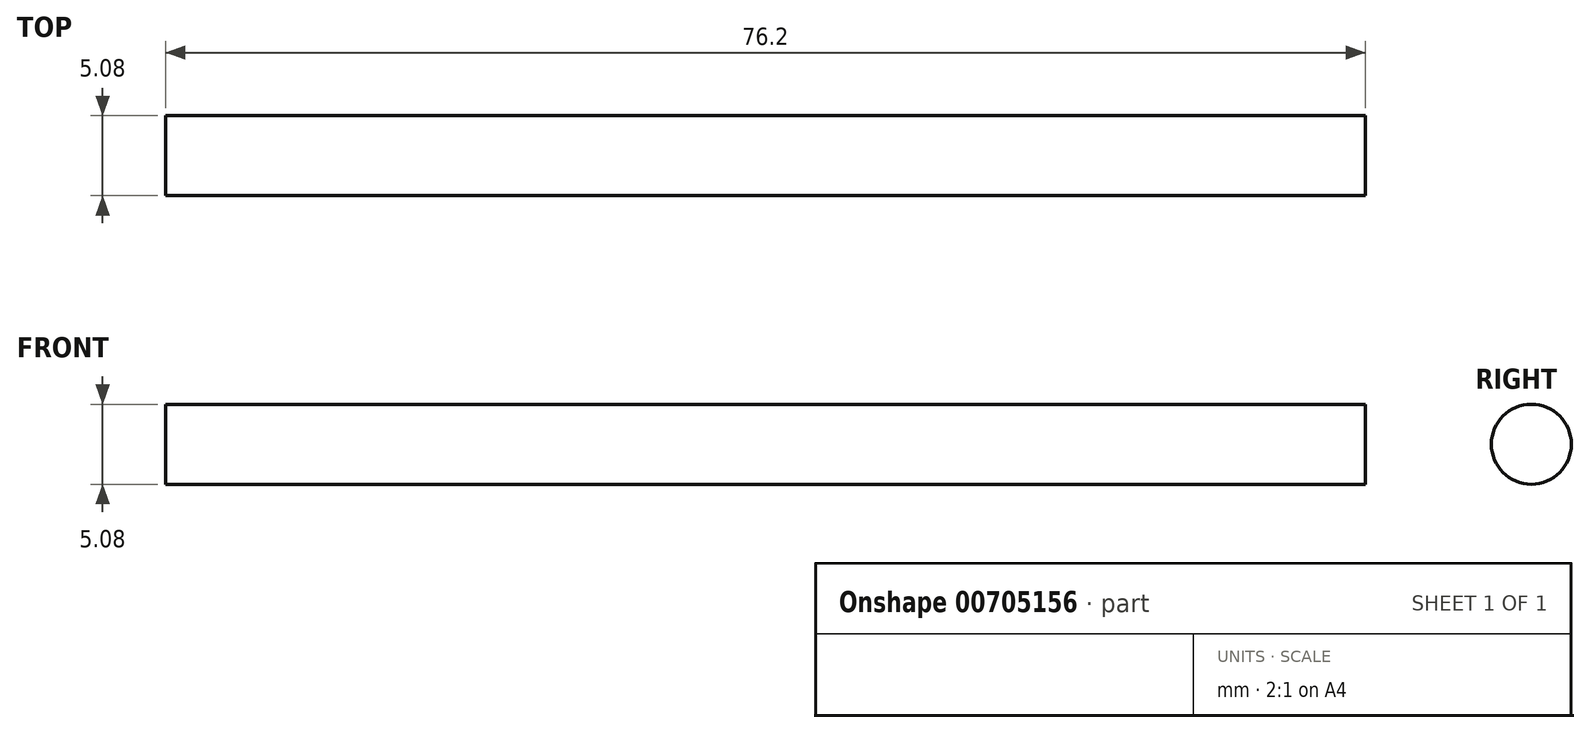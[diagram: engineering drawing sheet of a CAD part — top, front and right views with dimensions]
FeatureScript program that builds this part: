
annotation { "Feature Type Name" : "Feature", "Feature Type Description" : "" }
export const myFeature = defineFeature(function(context is Context, id is Id, definition is map)
    precondition{}
    {
        {
            var Q0;
            Q0=qCreatedBy(makeId("Front.planeOp"),FACE);
            var sketch = newSketch(context, id + "F0", { "sketchPlane" : qUnion([Q0])});
            skCircle(sketch, "E0", {"center": v(0, 0) * mm, "radius": 2.44 * mm});
            skSolve(sketch);
        }
        {
            var Q0;
            Q0=makeQuery(id+"F0.imprint","IMPRINT",FACE,{"disambiguationData":[TD([[makeQuery(id+"F0.imprint","IMPRINT",EDGE,{"derivedFrom":sQuery(id+"F0.wireOp",EDGE,"E0")}),1.0]])]});
            extrude(context, id + "F1", {"entities" : qUnion([Q0]), "depth" : 58.42 * mm, "offsetDistance" : 25.4 * mm});
        }
        {
            var Q0;
            Q0=makeQuery(id+"F1.opExtrude","SWEPT_BODY",BODY,{"disambiguationData":[OSD([sQuery(id+"F0.wireOp",EDGE,"E0")])]});
            deleteBodies(context, id + "F2", {"entities" : qUnion([Q0])});
        }
        {
            var Q0;
            Q0=qCreatedBy(makeId("Right.planeOp"),FACE);
            var sketch = newSketch(context, id + "F3", { "sketchPlane" : qUnion([Q0])});
            skCircle(sketch, "E1", {"center": v(0, 0) * mm, "radius": 2.54 * mm});
            skSolve(sketch);
        }
        {
            var Q0;
            Q0=makeQuery(id+"F3.imprint","IMPRINT",FACE,{"disambiguationData":[TD([[makeQuery(id+"F3.imprint","IMPRINT",EDGE,{"derivedFrom":sQuery(id+"F3.wireOp",EDGE,"E1")}),1.0]])]});
            extrude(context, id + "F4", {"entities" : qUnion([Q0]), "depth" : 76.2 * mm, "offsetDistance" : 25.4 * mm});
        }
    });
